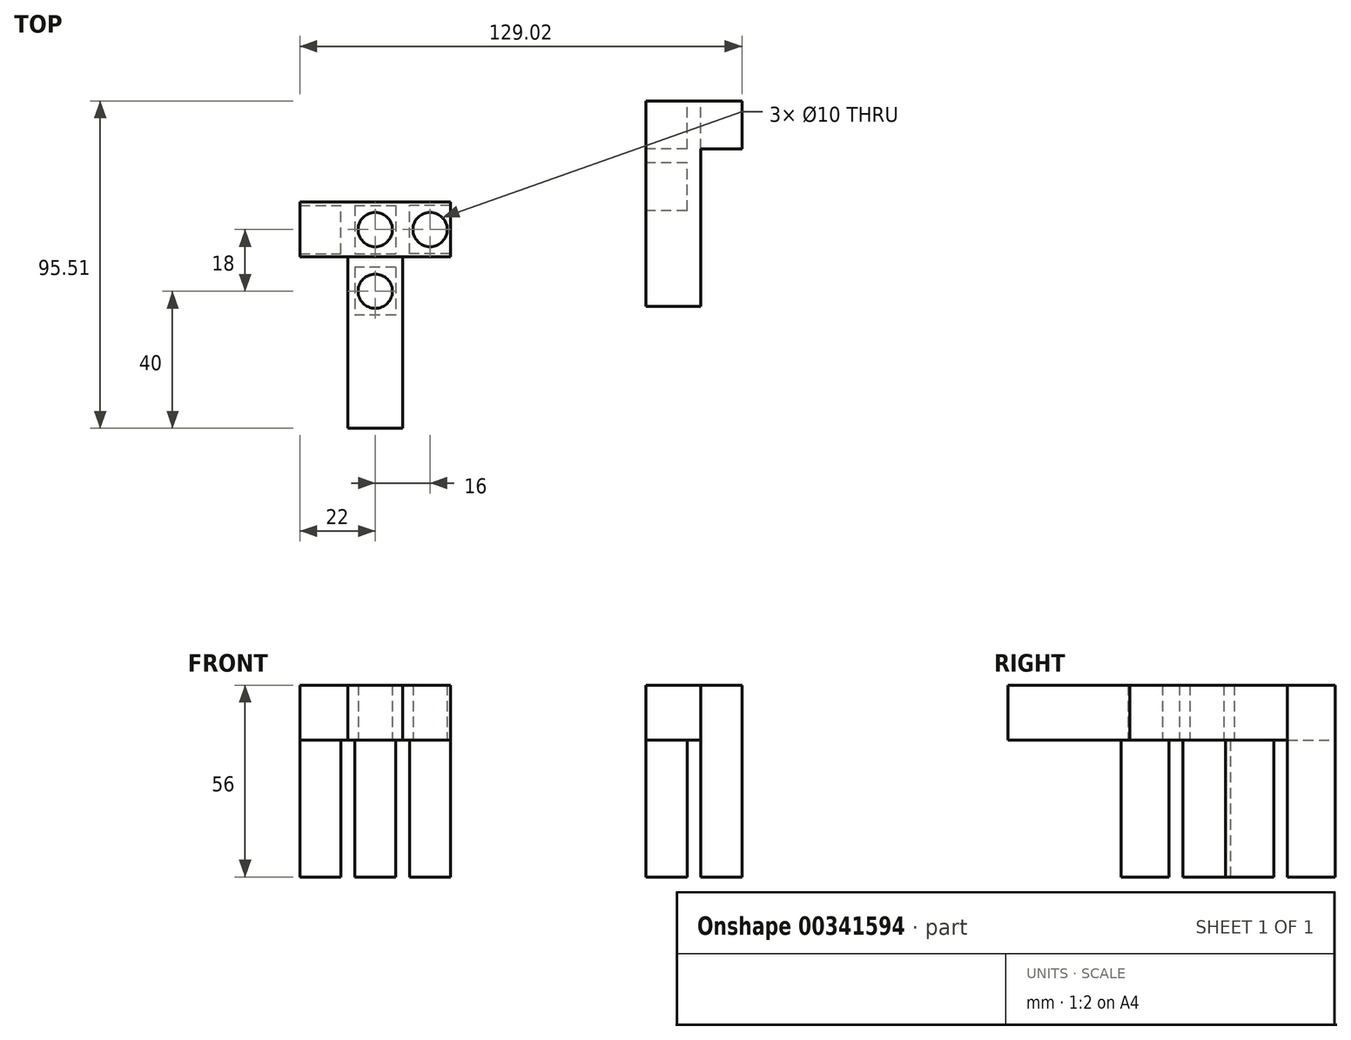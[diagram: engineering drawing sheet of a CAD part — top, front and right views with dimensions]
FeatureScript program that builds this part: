
annotation { "Feature Type Name" : "Feature", "Feature Type Description" : "" }
export const myFeature = defineFeature(function(context is Context, id is Id, definition is map)
    precondition{}
    {
        {
            var Q0;
            Q0=qCreatedBy(makeId("Top.planeOp"),FACE);
            var sketch = newSketch(context, id + "F0", { "sketchPlane" : qUnion([Q0])});
            skLineSegment(sketch, "E0.bottom", {"start": v(-6, 7) * mm, "end": v(6, 7) * mm});
            skLineSegment(sketch, "E0.top", {"start": v(-6, -7) * mm, "end": v(6, -7) * mm});
            skLineSegment(sketch, "E0.left", {"start": v(-6, 7) * mm, "end": v(-6, -7) * mm});
            skLineSegment(sketch, "E0.right", {"start": v(6, 7) * mm, "end": v(6, -7) * mm});
            skCircle(sketch, "E1", {"center": v(-16, 0) * mm, "radius": 5 * mm});
            skLineSegment(sketch, "E2.bottom", {"start": v(22, -8) * mm, "end": v(-22, -8) * mm});
            skLineSegment(sketch, "E2.top", {"start": v(22, 8) * mm, "end": v(-22, 8) * mm});
            skLineSegment(sketch, "E2.left", {"start": v(22, -8) * mm, "end": v(22, 8) * mm});
            skLineSegment(sketch, "E2.right", {"start": v(-22, -8) * mm, "end": v(-22, 8) * mm});
            skPoint(sketch, "E2.middle", {"position": v(0, 0) * mm});
            skLineSegment(sketch, "E3.bottom", {"start": v(22, -7) * mm, "end": v(10, -7) * mm});
            skLineSegment(sketch, "E3.top", {"start": v(22, 7) * mm, "end": v(10, 7) * mm});
            skLineSegment(sketch, "E3.left", {"start": v(22, -7) * mm, "end": v(22, 7) * mm});
            skLineSegment(sketch, "E3.right", {"start": v(10, -7) * mm, "end": v(10, 7) * mm});
            skPoint(sketch, "E3.middle", {"position": v(16, 0) * mm});
            skLineSegment(sketch, "E4", {"start": v(22, 0) * mm, "end": v(16, 0) * mm, "construction": true});
            skLineSegment(sketch, "E5", {"start": v(10, 0) * mm, "end": v(6, 0) * mm, "construction": true});
            skLineSegment(sketch, "E6", {"start": v(0, 20.06) * mm, "end": v(0, -66.52) * mm, "construction": true});
            skLineSegment(sketch, "E7.MirrorCS", {"start": v(-10, -7) * mm, "end": v(-10, 7) * mm});
            skLineSegment(sketch, "E8.MirrorCS", {"start": v(-22, 7) * mm, "end": v(-10, 7) * mm});
            skLineSegment(sketch, "E9.MirrorCS", {"start": v(-22, -7) * mm, "end": v(-10, -7) * mm});
            skLineSegment(sketch, "E10.MirrorCS", {"start": v(-22, -7) * mm, "end": v(-22, 7) * mm});
            skCircle(sketch, "E11", {"center": v(0, 0) * mm, "radius": 5 * mm});
            skCircle(sketch, "E12", {"center": v(16, 0) * mm, "radius": 5 * mm});
            skLineSegment(sketch, "E13.bottom", {"start": v(8, -58) * mm, "end": v(-8, -58) * mm});
            skLineSegment(sketch, "E13.top", {"start": v(8, -8) * mm, "end": v(-8, -8) * mm});
            skLineSegment(sketch, "E13.left", {"start": v(8, -58) * mm, "end": v(8, -8) * mm});
            skLineSegment(sketch, "E13.right", {"start": v(-8, -58) * mm, "end": v(-8, -8) * mm});
            skPoint(sketch, "E13.middle", {"position": v(0, -33) * mm});
            skLineSegment(sketch, "E14", {"start": v(0, -7) * mm, "end": v(0, -11) * mm, "construction": true});
            skCircle(sketch, "E15", {"center": v(0, -18) * mm, "radius": 5 * mm});
            skLineSegment(sketch, "E16.bottom", {"start": v(6, -11) * mm, "end": v(-6, -11) * mm});
            skLineSegment(sketch, "E16.top", {"start": v(6, -25) * mm, "end": v(-6, -25) * mm});
            skLineSegment(sketch, "E16.left", {"start": v(6, -11) * mm, "end": v(6, -25) * mm});
            skLineSegment(sketch, "E16.right", {"start": v(-6, -11) * mm, "end": v(-6, -25) * mm});
            skLineSegment(sketch, "E17.bottom", {"start": v(95.02, -22.49) * mm, "end": v(79.02, -22.49) * mm});
            skLineSegment(sketch, "E17.top", {"start": v(95.02, 37.51) * mm, "end": v(79.02, 37.51) * mm});
            skLineSegment(sketch, "E17.left", {"start": v(95.02, -22.49) * mm, "end": v(95.02, 37.51) * mm});
            skLineSegment(sketch, "E17.right", {"start": v(79.02, -22.49) * mm, "end": v(79.02, 37.51) * mm});
            skPoint(sketch, "E17.middle", {"position": v(87.02, 7.51) * mm});
            skLineSegment(sketch, "E18.bottom", {"start": v(183.87, 23.07) * mm, "end": v(167.87, 23.07) * mm});
            skLineSegment(sketch, "E18.top", {"start": v(183.87, 39.07) * mm, "end": v(167.87, 39.07) * mm});
            skLineSegment(sketch, "E18.left", {"start": v(183.87, 23.07) * mm, "end": v(183.87, 39.07) * mm});
            skLineSegment(sketch, "E18.right", {"start": v(167.87, 23.07) * mm, "end": v(167.87, 39.07) * mm});
            skPoint(sketch, "E18.middle", {"position": v(175.87, 31.07) * mm});
            skLineSegment(sketch, "E19.bottom", {"start": v(91.02, 5.51) * mm, "end": v(79.02, 5.51) * mm});
            skLineSegment(sketch, "E19.top", {"start": v(91.02, 19.51) * mm, "end": v(79.02, 19.51) * mm});
            skLineSegment(sketch, "E19.left", {"start": v(91.02, 5.51) * mm, "end": v(91.02, 19.51) * mm});
            skLineSegment(sketch, "E19.right", {"start": v(79.02, 5.51) * mm, "end": v(79.02, 19.51) * mm});
            skPoint(sketch, "E19.middle", {"position": v(85.02, 12.51) * mm});
            skLineSegment(sketch, "E20.bottom", {"start": v(182.03, -18.94) * mm, "end": v(196.03, -18.94) * mm});
            skLineSegment(sketch, "E20.top", {"start": v(182.03, -6.94) * mm, "end": v(196.03, -6.94) * mm});
            skLineSegment(sketch, "E20.left", {"start": v(182.03, -18.94) * mm, "end": v(182.03, -6.94) * mm});
            skLineSegment(sketch, "E20.right", {"start": v(196.03, -18.94) * mm, "end": v(196.03, -6.94) * mm});
            skPoint(sketch, "E20.middle", {"position": v(189.03, -12.94) * mm});
            skLineSegment(sketch, "E21.bottom", {"start": v(91.02, 23.51) * mm, "end": v(79.02, 23.51) * mm});
            skLineSegment(sketch, "E21.top", {"start": v(91.02, 37.51) * mm, "end": v(79.02, 37.51) * mm});
            skLineSegment(sketch, "E21.left", {"start": v(91.02, 23.51) * mm, "end": v(91.02, 37.51) * mm});
            skLineSegment(sketch, "E21.right", {"start": v(79.02, 23.51) * mm, "end": v(79.02, 37.51) * mm});
            skPoint(sketch, "E21.middle", {"position": v(85.02, 30.51) * mm});
            skLineSegment(sketch, "E22.bottom", {"start": v(107.02, 23.51) * mm, "end": v(95.02, 23.51) * mm});
            skLineSegment(sketch, "E22.top", {"start": v(107.02, 37.51) * mm, "end": v(95.02, 37.51) * mm});
            skLineSegment(sketch, "E22.left", {"start": v(107.02, 23.51) * mm, "end": v(107.02, 37.51) * mm});
            skLineSegment(sketch, "E22.right", {"start": v(95.02, 23.51) * mm, "end": v(95.02, 37.51) * mm});
            skPoint(sketch, "E22.middle", {"position": v(101.02, 30.51) * mm});
            skCircle(sketch, "E23", {"center": v(85.02, 30.51) * mm, "radius": 4 * mm});
            skLineSegment(sketch, "E24", {"start": v(85.02, 23.51) * mm, "end": v(85.02, 19.51) * mm, "construction": true});
            skCircle(sketch, "E25", {"center": v(85.02, 12.51) * mm, "radius": 4 * mm});
            skSolve(sketch);
        }
        {
            var Q0;
            Q0=makeQuery(id+"F0.imprint","IMPRINT",FACE,{"disambiguationData":[TD([[makeQuery(id+"F0.imprint","IMPRINT",EDGE,{"derivedFrom":sQuery(id+"F0.wireOp",EDGE,"E0.bottom")}),1.0]])]});
            var Q1;
            Q1=makeQuery(id+"F0.imprint","IMPRINT",FACE,{"disambiguationData":[TD([[makeQuery(id+"F0.imprint","IMPRINT",EDGE,{"derivedFrom":sQuery(id+"F0.wireOp",EDGE,"E1")}),-1.0]])]});
            var Q2;
            Q2=makeQuery(id+"F0.imprint","IMPRINT",FACE,{"disambiguationData":[TD([[makeQuery(id+"F0.imprint","IMPRINT",EDGE,{"derivedFrom":sQuery(id+"F0.wireOp",EDGE,"E0.bottom")}),-1.0]])]});
            var Q3;
            {var subQ1=sQuery(id+"F0.wireOp",EDGE,"E3.bottom");Q3=makeQuery(id+"F0.imprint","IMPRINT",FACE,{"disambiguationData":[TD([[makeQuery(id+"F0.imprint","IMPRINT",EDGE,{"derivedFrom":subQ1}),-1.0]])]});}
            extrude(context, id + "F1", {"entities" : qUnion([Q0, Q1, Q2, Q3]), "depth" : 16 * mm, "offsetDistance" : 25 * mm});
        }
        {
            var Q0;
            Q0=makeQuery(id+"F0.imprint","IMPRINT",FACE,{"disambiguationData":[TD([[makeQuery(id+"F0.imprint","IMPRINT",EDGE,{"derivedFrom":sQuery(id+"F0.wireOp",EDGE,"E1")}),-1.0]])]});
            var Q1;
            Q1=makeQuery(id+"F0.imprint","IMPRINT",FACE,{"disambiguationData":[TD([[makeQuery(id+"F0.imprint","IMPRINT",EDGE,{"derivedFrom":sQuery(id+"F0.wireOp",EDGE,"E0.bottom")}),-1.0]])]});
            var Q2;
            {var subQ1=sQuery(id+"F0.wireOp",EDGE,"E3.bottom");Q2=makeQuery(id+"F0.imprint","IMPRINT",FACE,{"disambiguationData":[TD([[makeQuery(id+"F0.imprint","IMPRINT",EDGE,{"derivedFrom":subQ1}),-1.0]])]});}
            var Q3;
            Q3=makeQuery(id+"F0.imprint","IMPRINT",FACE,{"disambiguationData":[TD([[makeQuery(id+"F0.imprint","IMPRINT",EDGE,{"derivedFrom":sQuery(id+"F0.wireOp",EDGE,"E15")}),-1.0]])]});
            var Q4;
            Q4=makeQuery(id+"F0.imprint","IMPRINT",FACE,{"disambiguationData":[TD([[makeQuery(id+"F0.imprint","IMPRINT",EDGE,{"derivedFrom":sQuery(id+"F0.wireOp",EDGE,"E12")}),1.0]])]});
            var Q5;
            Q5=makeQuery(id+"F0.imprint","IMPRINT",FACE,{"disambiguationData":[TD([[makeQuery(id+"F0.imprint","IMPRINT",EDGE,{"derivedFrom":sQuery(id+"F0.wireOp",EDGE,"E11")}),1.0]])]});
            var Q6;
            Q6=makeQuery(id+"F0.imprint","IMPRINT",FACE,{"disambiguationData":[TD([[makeQuery(id+"F0.imprint","IMPRINT",EDGE,{"derivedFrom":sQuery(id+"F0.wireOp",EDGE,"E1")}),1.0]])]});
            var Q7;
            Q7=makeQuery(id+"F0.imprint","IMPRINT",FACE,{"disambiguationData":[TD([[makeQuery(id+"F0.imprint","IMPRINT",EDGE,{"derivedFrom":sQuery(id+"F0.wireOp",EDGE,"E15")}),1.0]])]});
            extrude(context, id + "F2", {"entities" : qUnion([Q0, Q1, Q2, Q3, Q4, Q5, Q6, Q7]), "oppositeDirection" : true, "depth" : 40 * mm, "offsetDistance" : 25 * mm});
        }
        {
            var Q0;
            Q0=makeQuery(id+"F0.imprint","IMPRINT",FACE,{"disambiguationData":[TD([[makeQuery(id+"F0.imprint","IMPRINT",EDGE,{"derivedFrom":sQuery(id+"F0.wireOp",EDGE,"E13.bottom")}),-1.0]])]});
            var Q1;
            Q1=makeQuery(id+"F0.imprint","IMPRINT",FACE,{"disambiguationData":[TD([[makeQuery(id+"F0.imprint","IMPRINT",EDGE,{"derivedFrom":sQuery(id+"F0.wireOp",EDGE,"E15")}),-1.0]])]});
            extrude(context, id + "F3", {"entities" : qUnion([Q0, Q1]), "depth" : 16 * mm, "offsetDistance" : 25 * mm});
        }
        {
            var Q0;
            Q0=makeQuery(id+"F0.imprint","IMPRINT",FACE,{"disambiguationData":[TD([[makeQuery(id+"F0.imprint","IMPRINT",EDGE,{"derivedFrom":sQuery(id+"F0.wireOp",EDGE,"E1")}),1.0]])]});
            extrude(context, id + "F4", {"entities" : qUnion([Q0]), "operationType" : NewBodyOperationType.ADD, "depth" : 16 * mm, "offsetDistance" : 25 * mm});
        }
        {
            var Q0;
            {var subQ3=sQuery(id+"F0.wireOp",EDGE,"E17.bottom");Q0=makeQuery(id+"F0.imprint","IMPRINT",FACE,{"disambiguationData":[TD([[makeQuery(id+"F0.imprint","IMPRINT",EDGE,{"derivedFrom":subQ3}),-1.0]])]});}
            var Q1;
            {var subQ1=sQuery(id+"F0.wireOp",EDGE,"E19.bottom");Q1=makeQuery(id+"F0.imprint","IMPRINT",FACE,{"disambiguationData":[TD([[makeQuery(id+"F0.imprint","IMPRINT",EDGE,{"derivedFrom":subQ1}),-1.0]])]});}
            var Q2;
            {var subQ0=sQuery(id+"F0.wireOp",EDGE,"E21.bottom");Q2=makeQuery(id+"F0.imprint","IMPRINT",FACE,{"disambiguationData":[TD([[makeQuery(id+"F0.imprint","IMPRINT",EDGE,{"derivedFrom":subQ0}),-1.0]])]});}
            extrude(context, id + "F5", {"entities" : qUnion([Q0, Q1, Q2]), "depth" : 16 * mm, "offsetDistance" : 25 * mm});
        }
        {
            var Q0;
            {var subQ2=sQuery(id+"F0.wireOp",EDGE,"E22.bottom");Q0=makeQuery(id+"F0.imprint","IMPRINT",FACE,{"disambiguationData":[TD([[makeQuery(id+"F0.imprint","IMPRINT",EDGE,{"derivedFrom":subQ2}),-1.0]])]});}
            extrude(context, id + "F6", {"entities" : qUnion([Q0]), "depth" : 16 * mm, "offsetDistance" : 25 * mm});
        }
        {
            var Q0;
            {var subQ2=sQuery(id+"F0.wireOp",EDGE,"E22.bottom");Q0=makeQuery(id+"F0.imprint","IMPRINT",FACE,{"disambiguationData":[TD([[makeQuery(id+"F0.imprint","IMPRINT",EDGE,{"derivedFrom":subQ2}),-1.0]])]});}
            extrude(context, id + "F7", {"entities" : qUnion([Q0]), "operationType" : NewBodyOperationType.ADD, "oppositeDirection" : true, "depth" : 40 * mm, "offsetDistance" : 25 * mm});
        }
        {
            var Q0;
            {var subQ0=sQuery(id+"F0.wireOp",EDGE,"E21.bottom");Q0=makeQuery(id+"F0.imprint","IMPRINT",FACE,{"disambiguationData":[TD([[makeQuery(id+"F0.imprint","IMPRINT",EDGE,{"derivedFrom":subQ0}),-1.0]])]});}
            var Q1;
            Q1=makeQuery(id+"F0.imprint","IMPRINT",FACE,{"disambiguationData":[TD([[makeQuery(id+"F0.imprint","IMPRINT",EDGE,{"derivedFrom":sQuery(id+"F0.wireOp",EDGE,"E23")}),1.0]])]});
            extrude(context, id + "F8", {"entities" : qUnion([Q0, Q1]), "oppositeDirection" : true, "depth" : 40 * mm, "offsetDistance" : 25 * mm});
        }
        {
            var Q0;
            Q0=makeQuery(id+"F0.imprint","IMPRINT",FACE,{"disambiguationData":[TD([[makeQuery(id+"F0.imprint","IMPRINT",EDGE,{"derivedFrom":sQuery(id+"F0.wireOp",EDGE,"E23")}),1.0]])]});
            extrude(context, id + "F9", {"entities" : qUnion([Q0]), "operationType" : NewBodyOperationType.ADD, "depth" : 16 * mm, "offsetDistance" : 25 * mm});
        }
        {
            var Q0;
            Q0=makeQuery(id+"F0.imprint","IMPRINT",FACE,{"disambiguationData":[TD([[makeQuery(id+"F0.imprint","IMPRINT",EDGE,{"derivedFrom":sQuery(id+"F0.wireOp",EDGE,"E25")}),1.0]])]});
            var Q1;
            Q1=sQuery(id+"F0.wireOp",EDGE,"E25");
            extrude(context, id + "F10", {"entities" : qUnion([Q0]), "surfaceEntities" : qUnion([Q1]), "depth" : 16 * mm, "offsetDistance" : 25 * mm});
        }
        {
            var Q0;
            {var subQ1=sQuery(id+"F0.wireOp",EDGE,"E19.bottom");Q0=makeQuery(id+"F0.imprint","IMPRINT",FACE,{"disambiguationData":[TD([[makeQuery(id+"F0.imprint","IMPRINT",EDGE,{"derivedFrom":subQ1}),-1.0]])]});}
            var Q1;
            Q1=makeQuery(id+"F0.imprint","IMPRINT",FACE,{"disambiguationData":[TD([[makeQuery(id+"F0.imprint","IMPRINT",EDGE,{"derivedFrom":sQuery(id+"F0.wireOp",EDGE,"E25")}),1.0]])]});
            extrude(context, id + "F11", {"entities" : qUnion([Q0, Q1]), "operationType" : NewBodyOperationType.ADD, "oppositeDirection" : true, "depth" : 40 * mm, "offsetDistance" : 25 * mm});
        }
    });
